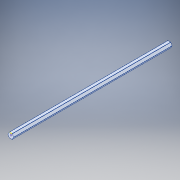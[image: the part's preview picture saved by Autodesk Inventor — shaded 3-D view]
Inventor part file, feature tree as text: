
AUTODESK INVENTOR PART (.ipt)
format: ipt  version: 2017 (Build 210142000, 142)  size: 133,632 bytes
history: native  units: in
note: dims shown in document units (in); Inventor stores cm internally (conversion verified against a paired STEP export)
features: sketch x3, split x1, fillet x1
ambient origin geometry x8: Origin, YZ Plane, XZ Plane, XY Plane, X Axis, Y Axis, Z Axis, Center Point
bodies: Solid1 (feature_tree)
feature tree (5):
  sketch  "Sketch1"
  split  "Split1"
  sketch  "Sketch3"
  sketch  "Sketch2"
  fillet  "Fillet1"  Radius=16.0in
